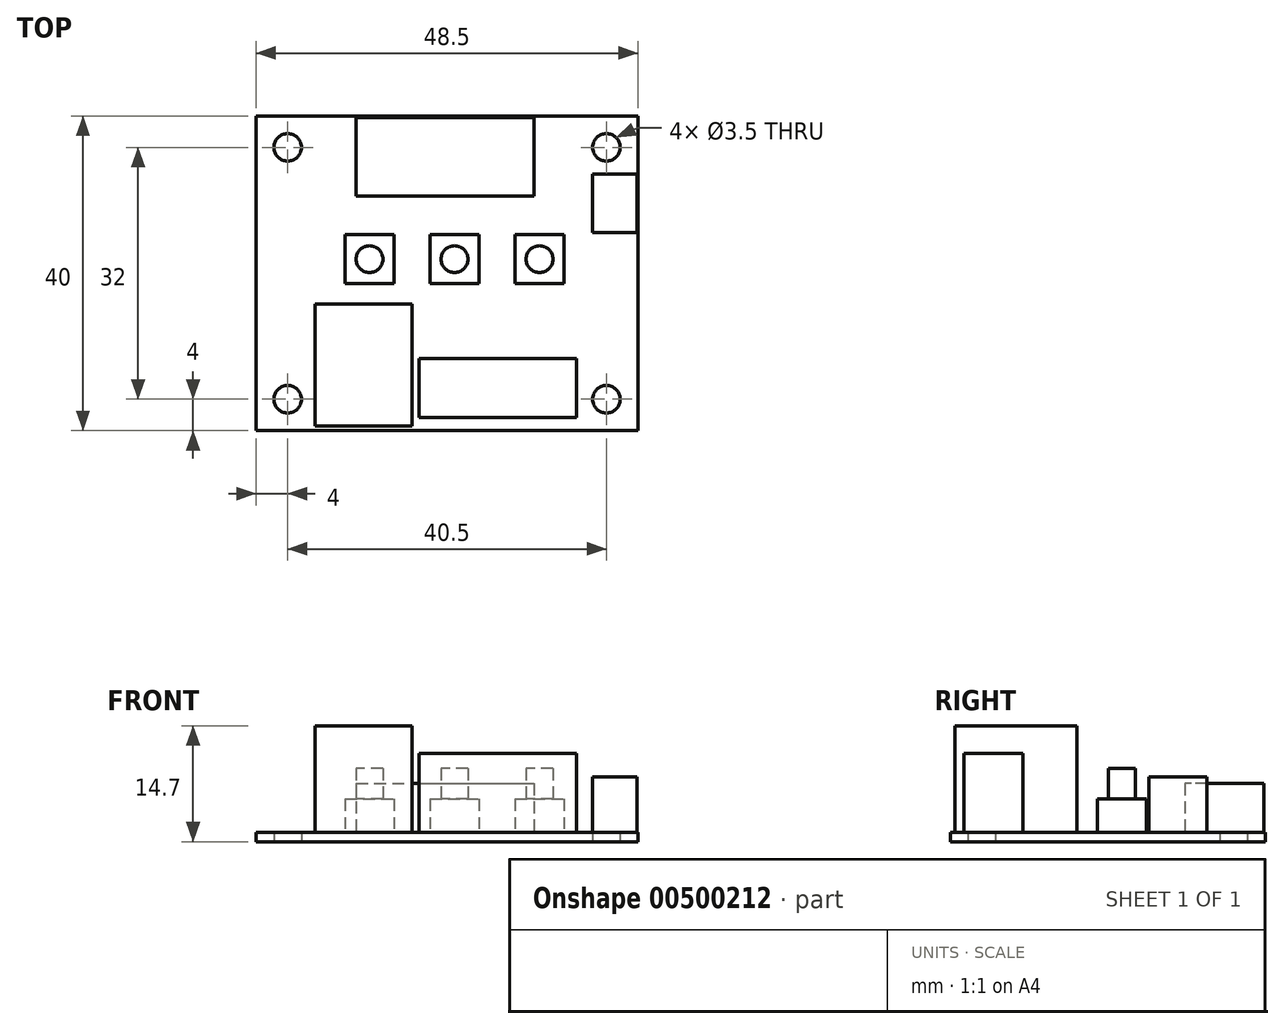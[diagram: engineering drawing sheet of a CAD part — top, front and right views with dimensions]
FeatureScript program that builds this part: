
annotation { "Feature Type Name" : "Feature", "Feature Type Description" : "" }
export const myFeature = defineFeature(function(context is Context, id is Id, definition is map)
    precondition{}
    {
        {
            var Q0;
            Q0=qCreatedBy(makeId("Top.planeOp"),FACE);
            var sketch = newSketch(context, id + "F0", { "sketchPlane" : qUnion([Q0])});
            skLineSegment(sketch, "E0.bottom", {"start": v(-24.25, 20) * mm, "end": v(24.25, 20) * mm});
            skLineSegment(sketch, "E0.top", {"start": v(-24.25, -20) * mm, "end": v(24.25, -20) * mm});
            skLineSegment(sketch, "E0.left", {"start": v(-24.25, 20) * mm, "end": v(-24.25, -20) * mm});
            skLineSegment(sketch, "E0.right", {"start": v(24.25, 20) * mm, "end": v(24.25, -20) * mm});
            skCircle(sketch, "E1", {"center": v(20.25, 16) * mm, "radius": 1.75 * mm});
            skCircle(sketch, "E2", {"center": v(20.25, -16) * mm, "radius": 1.75 * mm});
            skCircle(sketch, "E3", {"center": v(-20.25, 16) * mm, "radius": 1.75 * mm});
            skCircle(sketch, "E4", {"center": v(-20.25, -16) * mm, "radius": 1.75 * mm});
            skSolve(sketch);
        }
        {
            var Q0;
            Q0 = qSketchRegion(id + "F0", true);
            extrude(context, id + "F1", {"entities" : qUnion([Q0]), "depth" : 1.2 * mm});
        }
        {
            var Q0;
            Q0=makeQuery(id+"F1.opExtrude","CAP_FACE",FACE,{"disambiguationData":[OSD([sQuery(id+"F0.wireOp",EDGE,"E0.bottom"),sQuery(id+"F0.wireOp",EDGE,"E0.top"),sQuery(id+"F0.wireOp",EDGE,"E0.left"),sQuery(id+"F0.wireOp",EDGE,"E0.right"),sQuery(id+"F0.wireOp",EDGE,"E1"),sQuery(id+"F0.wireOp",EDGE,"E2"),sQuery(id+"F0.wireOp",EDGE,"E3"),sQuery(id+"F0.wireOp",EDGE,"E4")])],"isStart":false});
            var sketch = newSketch(context, id + "F2", { "sketchPlane" : qUnion([Q0])});
            skLineSegment(sketch, "E5.bottom", {"start": v(-11.55, 19.8) * mm, "end": v(11.05, 19.8) * mm});
            skLineSegment(sketch, "E5.top", {"start": v(-11.55, 9.8) * mm, "end": v(11.05, 9.8) * mm});
            skLineSegment(sketch, "E5.left", {"start": v(-11.55, 19.8) * mm, "end": v(-11.55, 9.8) * mm});
            skLineSegment(sketch, "E5.right", {"start": v(11.05, 19.8) * mm, "end": v(11.05, 9.8) * mm});
            skSolve(sketch);
        }
        {
            var Q0;
            Q0 = qSketchRegion(id + "F2", true);
            extrude(context, id + "F3", {"entities" : qUnion([Q0]), "operationType" : NewBodyOperationType.ADD, "depth" : 6.2 * mm});
        }
        {
            var Q0;
            Q0=makeQuery(id+"F1.opExtrude","CAP_FACE",FACE,{"disambiguationData":[OSD([sQuery(id+"F0.wireOp",EDGE,"E0.bottom"),sQuery(id+"F0.wireOp",EDGE,"E0.top"),sQuery(id+"F0.wireOp",EDGE,"E0.left"),sQuery(id+"F0.wireOp",EDGE,"E0.right"),sQuery(id+"F0.wireOp",EDGE,"E1"),sQuery(id+"F0.wireOp",EDGE,"E2"),sQuery(id+"F0.wireOp",EDGE,"E3"),sQuery(id+"F0.wireOp",EDGE,"E4")])],"isStart":false});
            var sketch = newSketch(context, id + "F4", { "sketchPlane" : qUnion([Q0])});
            skLineSegment(sketch, "E6.bottom", {"start": v(18.45, 12.6) * mm, "end": v(24.15, 12.6) * mm});
            skLineSegment(sketch, "E6.top", {"start": v(18.45, 5.2) * mm, "end": v(24.15, 5.2) * mm});
            skLineSegment(sketch, "E6.left", {"start": v(18.45, 12.6) * mm, "end": v(18.45, 5.2) * mm});
            skLineSegment(sketch, "E6.right", {"start": v(24.15, 12.6) * mm, "end": v(24.15, 5.2) * mm});
            skSolve(sketch);
        }
        {
            var Q0;
            Q0 = qSketchRegion(id + "F4", true);
            extrude(context, id + "F5", {"entities" : qUnion([Q0]), "operationType" : NewBodyOperationType.ADD, "depth" : 7 * mm, "offsetDistance" : 25 * mm});
        }
        {
            var Q0;
            Q0=makeQuery(id+"F1.opExtrude","CAP_FACE",FACE,{"disambiguationData":[OSD([sQuery(id+"F0.wireOp",EDGE,"E0.bottom"),sQuery(id+"F0.wireOp",EDGE,"E0.top"),sQuery(id+"F0.wireOp",EDGE,"E0.left"),sQuery(id+"F0.wireOp",EDGE,"E0.right"),sQuery(id+"F0.wireOp",EDGE,"E1"),sQuery(id+"F0.wireOp",EDGE,"E2"),sQuery(id+"F0.wireOp",EDGE,"E3"),sQuery(id+"F0.wireOp",EDGE,"E4")])],"isStart":false});
            var sketch = newSketch(context, id + "F6", { "sketchPlane" : qUnion([Q0])});
            skLineSegment(sketch, "E7.bottom", {"start": v(-3.55, -10.8) * mm, "end": v(16.45, -10.8) * mm});
            skLineSegment(sketch, "E7.top", {"start": v(-3.55, -18.3) * mm, "end": v(16.45, -18.3) * mm});
            skLineSegment(sketch, "E7.left", {"start": v(-3.55, -10.8) * mm, "end": v(-3.55, -18.3) * mm});
            skLineSegment(sketch, "E7.right", {"start": v(16.45, -10.8) * mm, "end": v(16.45, -18.3) * mm});
            skSolve(sketch);
        }
        {
            var Q0;
            Q0 = qSketchRegion(id + "F6", true);
            extrude(context, id + "F7", {"entities" : qUnion([Q0]), "operationType" : NewBodyOperationType.ADD, "depth" : 10 * mm});
        }
        {
            var Q0;
            Q0=makeQuery(id+"F1.opExtrude","CAP_FACE",FACE,{"disambiguationData":[OSD([sQuery(id+"F0.wireOp",EDGE,"E0.bottom"),sQuery(id+"F0.wireOp",EDGE,"E0.top"),sQuery(id+"F0.wireOp",EDGE,"E0.left"),sQuery(id+"F0.wireOp",EDGE,"E0.right"),sQuery(id+"F0.wireOp",EDGE,"E1"),sQuery(id+"F0.wireOp",EDGE,"E2"),sQuery(id+"F0.wireOp",EDGE,"E3"),sQuery(id+"F0.wireOp",EDGE,"E4")])],"isStart":false});
            var sketch = newSketch(context, id + "F8", { "sketchPlane" : qUnion([Q0])});
            skLineSegment(sketch, "E8.bottom", {"start": v(-16.75, -3.9) * mm, "end": v(-4.45, -3.9) * mm});
            skLineSegment(sketch, "E8.top", {"start": v(-16.75, -19.4) * mm, "end": v(-4.45, -19.4) * mm});
            skLineSegment(sketch, "E8.left", {"start": v(-16.75, -3.9) * mm, "end": v(-16.75, -19.4) * mm});
            skLineSegment(sketch, "E8.right", {"start": v(-4.45, -3.9) * mm, "end": v(-4.45, -19.4) * mm});
            skSolve(sketch);
        }
        {
            var Q0;
            Q0 = qSketchRegion(id + "F8", true);
            extrude(context, id + "F9", {"entities" : qUnion([Q0]), "operationType" : NewBodyOperationType.ADD, "depth" : 13.5 * mm});
        }
        {
            var Q0;
            Q0=makeQuery(id+"F1.opExtrude","CAP_FACE",FACE,{"disambiguationData":[OSD([sQuery(id+"F0.wireOp",EDGE,"E0.bottom"),sQuery(id+"F0.wireOp",EDGE,"E0.top"),sQuery(id+"F0.wireOp",EDGE,"E0.left"),sQuery(id+"F0.wireOp",EDGE,"E0.right"),sQuery(id+"F0.wireOp",EDGE,"E1"),sQuery(id+"F0.wireOp",EDGE,"E2"),sQuery(id+"F0.wireOp",EDGE,"E3"),sQuery(id+"F0.wireOp",EDGE,"E4")])],"isStart":false});
            var sketch = newSketch(context, id + "F10", { "sketchPlane" : qUnion([Q0])});
            skLineSegment(sketch, "E9.bottom", {"start": v(8.65, 4.9) * mm, "end": v(14.85, 4.9) * mm});
            skLineSegment(sketch, "E9.top", {"start": v(8.65, -1.3) * mm, "end": v(14.85, -1.3) * mm});
            skLineSegment(sketch, "E9.left", {"start": v(8.65, 4.9) * mm, "end": v(8.65, -1.3) * mm});
            skLineSegment(sketch, "E9.right", {"start": v(14.85, 4.9) * mm, "end": v(14.85, -1.3) * mm});
            skLineSegment(sketch, "E10.bottom", {"start": v(-2.15, 4.9) * mm, "end": v(4.05, 4.9) * mm});
            skLineSegment(sketch, "E10.top", {"start": v(-2.15, -1.3) * mm, "end": v(4.05, -1.3) * mm});
            skLineSegment(sketch, "E10.left", {"start": v(-2.15, 4.9) * mm, "end": v(-2.15, -1.3) * mm});
            skLineSegment(sketch, "E10.right", {"start": v(4.05, 4.9) * mm, "end": v(4.05, -1.3) * mm});
            skLineSegment(sketch, "E11.bottom", {"start": v(-12.95, 4.9) * mm, "end": v(-6.75, 4.9) * mm});
            skLineSegment(sketch, "E11.top", {"start": v(-12.95, -1.3) * mm, "end": v(-6.75, -1.3) * mm});
            skLineSegment(sketch, "E11.left", {"start": v(-12.95, 4.9) * mm, "end": v(-12.95, -1.3) * mm});
            skLineSegment(sketch, "E11.right", {"start": v(-6.75, 4.9) * mm, "end": v(-6.75, -1.3) * mm});
            skCircle(sketch, "E12", {"center": v(-9.85, 1.8) * mm, "radius": 1.7 * mm});
            skCircle(sketch, "E13", {"center": v(0.95, 1.8) * mm, "radius": 1.7 * mm});
            skCircle(sketch, "E14", {"center": v(11.75, 1.8) * mm, "radius": 1.7 * mm});
            skSolve(sketch);
        }
        {
            var Q0;
            Q0 = qSketchRegion(id + "F10", true);
            extrude(context, id + "F11", {"entities" : qUnion([Q0]), "operationType" : NewBodyOperationType.ADD, "depth" : 4.2 * mm});
        }
        {
            var Q0;
            Q0=makeQuery(id+"F11.boolean.opBoolean","SPLIT",FACE,{"disambiguationData":[TD([makeQuery(id+"F11.opExtrude","SWEPT_FACE",FACE,{"disambiguationData":[OSD([sQuery(id+"F10.wireOp",EDGE,"E12")])]})])],"derivedFrom":makeQuery(id+"F1.opExtrude","CAP_FACE",FACE,{"disambiguationData":[OSD([sQuery(id+"F0.wireOp",EDGE,"E0.bottom"),sQuery(id+"F0.wireOp",EDGE,"E0.top"),sQuery(id+"F0.wireOp",EDGE,"E0.left"),sQuery(id+"F0.wireOp",EDGE,"E0.right"),sQuery(id+"F0.wireOp",EDGE,"E1"),sQuery(id+"F0.wireOp",EDGE,"E2"),sQuery(id+"F0.wireOp",EDGE,"E3"),sQuery(id+"F0.wireOp",EDGE,"E4")])],"isStart":false})});
            var Q1;
            Q1=makeQuery(id+"F11.boolean.opBoolean","SPLIT",FACE,{"disambiguationData":[TD([makeQuery(id+"F11.opExtrude","SWEPT_FACE",FACE,{"disambiguationData":[OSD([sQuery(id+"F10.wireOp",EDGE,"E13")])]})])],"derivedFrom":makeQuery(id+"F1.opExtrude","CAP_FACE",FACE,{"disambiguationData":[OSD([sQuery(id+"F0.wireOp",EDGE,"E0.bottom"),sQuery(id+"F0.wireOp",EDGE,"E0.top"),sQuery(id+"F0.wireOp",EDGE,"E0.left"),sQuery(id+"F0.wireOp",EDGE,"E0.right"),sQuery(id+"F0.wireOp",EDGE,"E1"),sQuery(id+"F0.wireOp",EDGE,"E2"),sQuery(id+"F0.wireOp",EDGE,"E3"),sQuery(id+"F0.wireOp",EDGE,"E4")])],"isStart":false})});
            var Q2;
            Q2=makeQuery(id+"F11.boolean.opBoolean","SPLIT",FACE,{"disambiguationData":[TD([makeQuery(id+"F11.opExtrude","SWEPT_FACE",FACE,{"disambiguationData":[OSD([sQuery(id+"F10.wireOp",EDGE,"E14")])]})])],"derivedFrom":makeQuery(id+"F1.opExtrude","CAP_FACE",FACE,{"disambiguationData":[OSD([sQuery(id+"F0.wireOp",EDGE,"E0.bottom"),sQuery(id+"F0.wireOp",EDGE,"E0.top"),sQuery(id+"F0.wireOp",EDGE,"E0.left"),sQuery(id+"F0.wireOp",EDGE,"E0.right"),sQuery(id+"F0.wireOp",EDGE,"E1"),sQuery(id+"F0.wireOp",EDGE,"E2"),sQuery(id+"F0.wireOp",EDGE,"E3"),sQuery(id+"F0.wireOp",EDGE,"E4")])],"isStart":false})});
            extrude(context, id + "F12", {"entities" : qUnion([Q0, Q1, Q2]), "operationType" : NewBodyOperationType.ADD, "depth" : 8.1 * mm});
        }
    });
